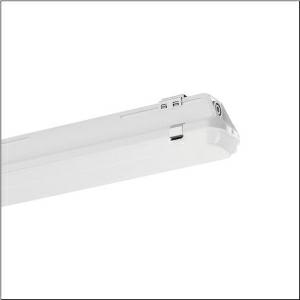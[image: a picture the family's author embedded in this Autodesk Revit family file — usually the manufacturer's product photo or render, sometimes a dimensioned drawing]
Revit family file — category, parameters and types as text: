
# Revit family: monsun_r__12_emergency_51fp20dp460hr_2cd6
name_source: partatom
category: Lighting Fixtures
units: mm (PartAtom-declared; Revit-internal decimal feet)

## family parameters
Cut with Voids When Loaded = No
Host = Face
Light Source = No
Part Type = Normal
Room Calculation Point = No
Round Connector Dimension = Use Diameter
Shared = No

## types (1)
- --- (1 x LED, 800 lm, 6.9 W, 4000K)
    Apparent Load = 7 VA
    CIE Flux Codes = 45 75 93 94 100
    Color Rendering = 80
    Color Temperature = 4000K
    Default Elevation = 1800 mm
    Description = Monsun® 12 emergency, damp-proof luminaire, chain hanger, primary optical cover: enclosure, of PC, light emission: direct distribution, primary light characteristic: symmetric, installation type: suspended mounting, surface-mounted, horizontal mounting, vertical mounting, LED rated luminous flux: 5.450 lm, light colour: 840, colour temperature: 4000K, control gear: ECG DALI, with terminal, 5+2-pole, max. 2.5mm², mains connection: 220..240V, AC/DC, 0/50..60Hz, rated input power: 35W, changeover relay for equivalent power supply, AC/DC, 0/50..60Hz, luminaire housing, of glass-fibre reinforced polyester, uncoated, bright grey, length: 1.590 mm, width: 90 mm, height: 88mm, clip for enclosure, of stainless steel (V2A), ceiling mounting element, of stainless steel (V2A), chain hanger, of stainless steel (V2A), protection rating (complete): IP66, insulation class (complete): insulation class I (protective earthing), certification: CE, protection symbol: D, impact resistance: IK08, permissible ambient temperature for indoor applications: -25..+35°C, standard: EN 50419, EN 60598-2-1, EN 60598-2-22, no direct snow, no direct sun, no direct rain, for indoor or canopied outdoor use, corresponds to IFS (International Featured Standards) requirements for safety and quality in the food industry, packaging unit: 1 piece
    Height = 89 mm
    Lamp = 1 x LED
    Lamp Light Flux = 800 lm
    Lamp Power = 6.9 W
    Lamp count = 1
    Length = 1590 mm
    Luminous efficacy = 116 lm/W
    Manufacturer = Siteco
    ModVariant = No
    Model = 51FP20DP460HR
    Mounting Place = Ceiling
    Mounting Type = Pendant
    Number of Poles = 1
    OnlyDefault = Yes
    Power Factor = 1
    Product Name = Monsun® 12 emergency
    Product group = damp-proof luminaire | ceiling pendant
    ProductGroupID = 908
    Protection Class = Protection class I
    Protection Degree = IP 66
    RLX_Detail_Level = 1
    RlxData = <blob elided: 92321 chars, md5=3dd138f8>
    Socket = socket
    Standby Power = 0 W
    System Light Flux = 800 lm
    System Power = 7 W
    Type Comments = : equivalent power supply (DC)
    Type Image = l_1004748.jpg
    URL = http://relux.com
    VarID = @adj_125629
    Voltage = 0 V
    Weight = 0.00 kg
    Width = 90 mm

## geometry (parser evidence)
native form markers: Blend x4, Sweep x13
no freeform markers — native parametric forms only
